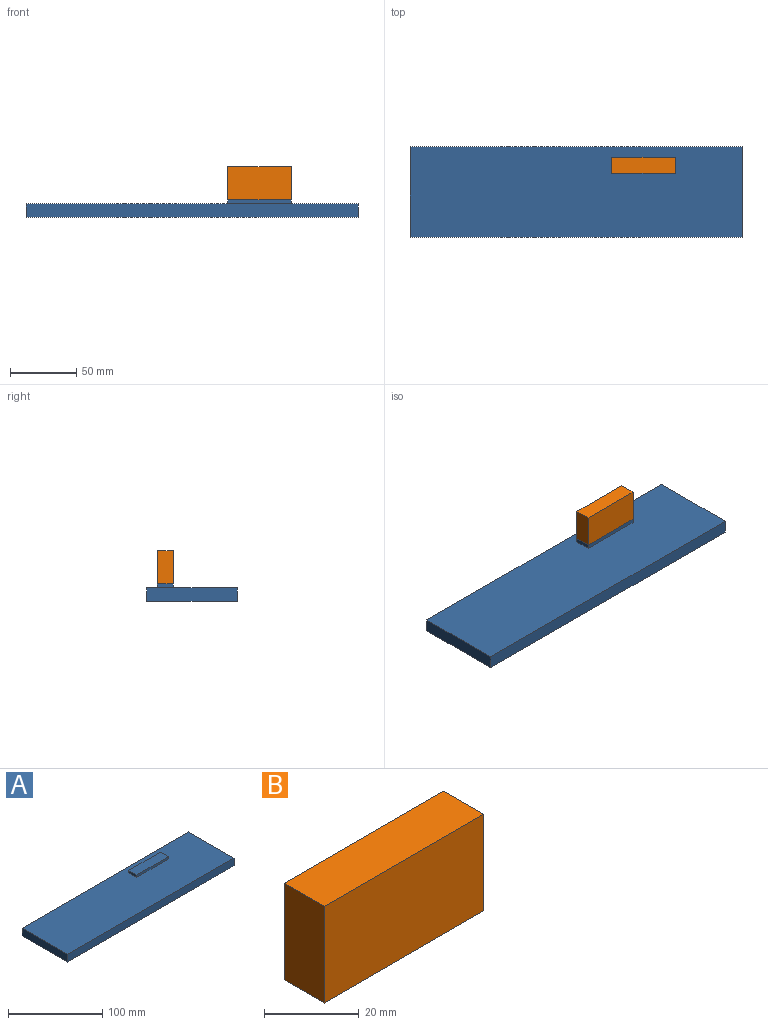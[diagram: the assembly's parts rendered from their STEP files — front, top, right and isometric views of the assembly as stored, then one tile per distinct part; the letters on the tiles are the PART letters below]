
ASSEMBLY  parts=2 mates=1
PART A: 11 faces, bbox 250x68x13 mm
  f0: plane 250x67.98mm, normal (0,0,1), area 16422.4mm2, adj f1,f2,f3,f4,f6,f7,f8,f9
  f1: plane 250x10mm, normal (0,1,0), area 2500mm2, adj f0,f2,f4,f5
  f2: plane 67.98x10mm, normal (-1,0,0), area 679.8mm2, adj f0,f1,f3,f5
  f3: plane 250x10mm, normal (0,-1,0), area 2500mm2, adj f0,f2,f4,f5
  f4: plane 67.98x10mm, normal (1,0,0), area 679.8mm2, adj f0,f1,f3,f5
  f5: plane 250x67.98mm, normal (0,0,-1), area 16996mm2, adj f1,f2,f3,f4
  f6: plane 47.8x3mm, normal (0,1,0), area 143.4mm2, adj f0,f7,f9,f10
  f7: plane 12x3mm, normal (-1,0,0), area 36mm2, adj f0,f6,f8,f10
  f8: plane 47.8x3mm, normal (0,-1,0), area 143.4mm2, adj f0,f7,f9,f10
  f9: plane 12x3mm, normal (1,0,0), area 36mm2, adj f0,f6,f8,f10
  f10: plane 47.8x12mm, normal (0,0,1), area 573.6mm2, adj f6,f7,f8,f9
PART B: 6 faces, bbox 47.8x12x25 mm
  f0: plane 47.8x25mm, normal (0,1,0), area 1195mm2, adj f1,f3,f4,f5
  f1: plane 25x12mm, normal (-1,0,0), area 300mm2, adj f0,f2,f4,f5
  f2: plane 47.8x25mm, normal (0,-1,0), area 1195mm2, adj f1,f3,f4,f5
  f3: plane 25x12mm, normal (1,0,0), area 300mm2, adj f0,f2,f4,f5
  f4: plane 47.8x12mm, normal (0,0,1), area 573.6mm2, adj f0,f1,f2,f3
  f5: plane 47.8x12mm, normal (0,0,-1), area 573.6mm2, adj f0,f1,f2,f3
PLACE A t=(-40.64,-47.17,-10.57)mm
PLACE B t=(-40.64,-17.17,-7.57)mm
MATE fastened B.f5 <-> A.f10  axis (0,0,-1) through (10.2,-27.18,2.43)mm
